# Revit family: IS_Linda-X_T4753_BIM_NL
name_source: partatom
category: Plumbing Fixtures
units: mm (PartAtom-declared; Revit-internal decimal feet)

## family parameters
Always vertical = No
Cut with Voids When Loaded = No
OmniClass Number = 23.39.29.13.21.19
Part Type = Normal
Room Calculation Point = No
Round Connector Dimension = Use Diameter
Shared = No
Work Plane-Based = No

## types (5) — shared parameters
Accesoires = https://www.idealstandard.nl
Accessories = https://www.idealstandard.nl
Afmetingen = 480 x 135 x 500mm
AfstandsEenheid = Millimeter
AreaUnits = Millimeter
Artikelomschrijving = Linda-X Waschbecken 50cm, 1 Hahnloch, mit Schlitzüberlauf
Artikelreferentie = Linda-X Basin 50cm, 1 Tap Hole, Slotted Overflow
Auteur = Idea Standard
BIMObjectName = IS_IdealStandard_Wallhungwashbasins_Linda-X_T4753
BIMobject category = Sanitary Basins
BIMobject category code = sanitary-basins
BIMobject main category = Sanitary
BIMobject main category code = sanitary
Beschrijvinggarantie = Herstellergarantie
BimObjectNaam = IS_IdealStandard_Wallhungwashbasins_Linda-X_T4753
Brand = Idea Standard
Brand url = http://www.idealstandard.nl
ConnectionType = Plumbing
CurrencyUnit = €
CurrentRevision = 1
Date of publishing = 14/07/2021
Description = Linda-X Waschbecken 50cm, 1 Hahnloch, mit Schlitzüberlauf
DurationUnit = Years
DuurEenheid = Jahre
Edition number = 1
Eigenschappen = Waschbecken 50cm, 1 Hahnloch, mit Schlitzüberlauf
ElementType = Fixed
Features = Waschbecken 50cm, 1 Hahnloch, mit Schlitzüberlauf
Garantieunits = Jahren
Help = https://www.idealstandard.nl
Hoogte = 135.05197
Hulp = https://www.idealstandard.nl
IFC Classification = Sanitary Terminal
IfcExportAs = IfcSanitaryTerminalType
IfcExportType = WASHHANDBASIN
Installatieinstructies = https://www.idealstandard.nl
Installation instructions = https://www.idealstandard.nl
InstallationInstructions = https://www.idealstandard.nl
Lengte = 480 mm
LinearUnits = Millimetres
MaintenanceInformation = https://www.idealstandard.nl
Manufacturer = Ideal Standard
Manufacturer name = Ideal Standard
ManufacturerURL = https://www.idealstandard.nl
Masterformat 2014 Code = 33 44 13.13
Masterformat 2014 Description = Catchbasins
Materiaal = Keramik
Material = Diamatec
Material main = Keramik
Merk = Ideal Standard
ModelReference = Linda-X Basin 50cm, 1 Tap Hole, Slotted Overflow
Montageinstuctie = https://www.idealstandard.nl
NBS Reference Code = 45-35-70/369
NBS Reference Description = Wall hung wash basins
Name = Wallhungwashbasins_Linda-X_T4753_IdealStandard
NettWeight = 13.5
NominalDepth = 480 mm
NominalHeight = 135 mm  [stored 0.442913 ft]
NominalWidth = 500 mm
Normen = Wallhungwashbasins_Linda-X_T4753_IdealStandard
OmniClass Code = 23-39 29 13 21 19
OmniClass Description = Surface Water Retention Basins
Ophangingwastafel = Wand oder Sockel installiert
OppervlakteEenheid = Millimeter
Product Guid = 67c275e4-bc2d-4785-9b63-4539ee6b2bc2
Product SKU = T4753
Product certification = https://www.idealstandard.nl
Product data url = https://bimobject.com
Product family = Linda-X
Product group = Washbasins
Product name = Linda-X Basin 50cm, 1 Tap Hole, with Slotted Overflow
Product url = https://www.idealstandard.nl
ProductInformation = https://www.idealstandard.nl
Productinformatie = https://www.idealstandard.nl
QR code = http://bimobject.com
Referentie = Linda-X Basin 50cm, 1 Tap Hole, with Slotted Overflow
Revisie = 1
Size = 480 x 135 x 500mm
Space = Internal
SpareParts = https://www.idealstandard.nl
Technical description = https://www.idealstandard.nl
Telefoonnummer = 077 355 08 08
Typeconnectie = Installation
UNSPSC Code = 301815
URL = https://www.idealstandard.nl
Uniclass 1.4 Code = L7212
Uniclass 1.4 Description = Washbasins
Uniclass 2.0 Code = PR-31-79
Uniclass 2.0 Description = Sinks, Wash Basins And Troughs
Uniclass 2015 Code = Pr_40_20_96_96
Uniclass 2015 Name = Wall-hung washbasins
Uniclass2015Beschrijving = Wall-hung washbasins
Uniclass2015Code = Pr_40_20_96_96
Uniclass2015Referentie = Pr_40_20_96_96
Uniclass2015Title = Wall-hung washbasins
Uniclass2015Version = v1.20
Urlproducent = https://www.idealstandard.nl
ValutaEenheid = €
Versie = 1
Version = 1
VolumeUnits = Litres
Volumeunits = Liter
WRASURL = https://www.wrasapprovals.co.uk
WarrantyDescription = Manufacturer Warranty
WarrantyDurationUnit = 5
WashHandBasinMounting = Wall Hung
WashHandBasinType = Wall Hung Wash Basin
Wisselstukken = https://www.idealstandard.nl
Youtube clip = https://www.youtube.com
zero-valued in all types: Breedte, BrutoGewicht, Cost, Diepte, MaterialThickness, Nettogewicht, OutletConnectionSize, Vervangingskosten

## per-type parameters (varying)
| type | Afwerking | Artikelnummer | BarCode | Barcode | Color | Finish | GTIN code | Kleur | MainColor | Model | ModelNumber | Shape | Typewastafel | Vorm |
| T475301 - Linda-X Basin 50cm, 1 Tap Hole, with Slotted Overflow - Gloss White | Glänzend weiß | T475301 | 8014140488064 | 8014140488064 | Glänzend weiß | Glänzend weiß | https://8014140488064 | Glänzend weiß | White | T475301 | T475301 | Rechteckig | Rechteckig, Wand oder Sockel installiert | Rechteckig |
| T4753MA - Linda-X Basin 50cm, 1 Tap Hole, with Slotted Overflow - Ideal Plus White | IdealPlusWeiß | T4753MA | 8014140490432 | 8014140490432 | IdealPlusWeiß | IdealPlusWeiß | https://8014140490432 | IdealPlusWeiß | Ideal Plus White | T4753MA | T4753MA | Rechteckig | Rechteckig, Wand oder Sockel installiert | Rechteckig |
| T4753V2 - Linda-X Basin 50cm, 1 Tap Hole, with Slotted Overflow - Black Gloss | SchwarzGlanz | T4753V2 |  |  | SchwarzGlanz | SchwarzGlanz |  | SchwarzGlanz | Black Gloss | T4753V2 | T4753V2 | #N / A | #N / A, Wand oder Sockel installiert | #N / A |
| T4753V3 - Linda-X Basin 50cm, 1 Tap Hole, with Slotted Overflow - Silk Black | SeideSchwarz | T4753V3 |  |  | SeideSchwarz | SeideSchwarz |  | SeideSchwarz | Silk Black | T4753V3 | T4753V3 | Rechteckig | Rechteckig, Wand oder Sockel installiert | Rechteckig |
| T4753V9 - Linda-X Basin 50cm, 1 Tap Hole, with Slotted Overflow - Concrete | Beton | T4753V9 |  |  | Beton | Beton |  | Beton | Concrete | T4753V9 | T4753V9 | Rechteckig | Rechteckig, Wand oder Sockel installiert | Rechteckig |

note: [stored X ft] marks values corroborated as IEEE doubles in the binary element streams (Revit-internal decimal feet)

## geometry (parser evidence)
native form markers: Sweep x4
no freeform markers — native parametric forms only
